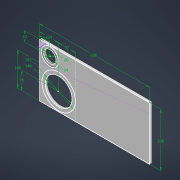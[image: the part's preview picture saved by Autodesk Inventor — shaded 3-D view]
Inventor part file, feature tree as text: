
AUTODESK INVENTOR PART (.ipt)
format: ipt  version: 2022 (Build 260153000, 153)  size: 133,120 bytes
history: native  units: mm
features: other x4, extrude x2, sketch x1
ambient origin geometry x8: Origin, YZ Plane, XZ Plane, XY Plane, X Axis, Y Axis, Z Axis, Center Point
bodies: Body1 (feature_tree)
feature tree (7):
  other  "Твердое тело1"
  other  "Front0"
  extrude  "Выдавливание2"  Depth=600.0mm
  other  "РабПлоскость9"
  other  "Разделение5"
  extrude  "Выдавливание7"  Depth=290.0mm
  sketch  "Эскиз7"
